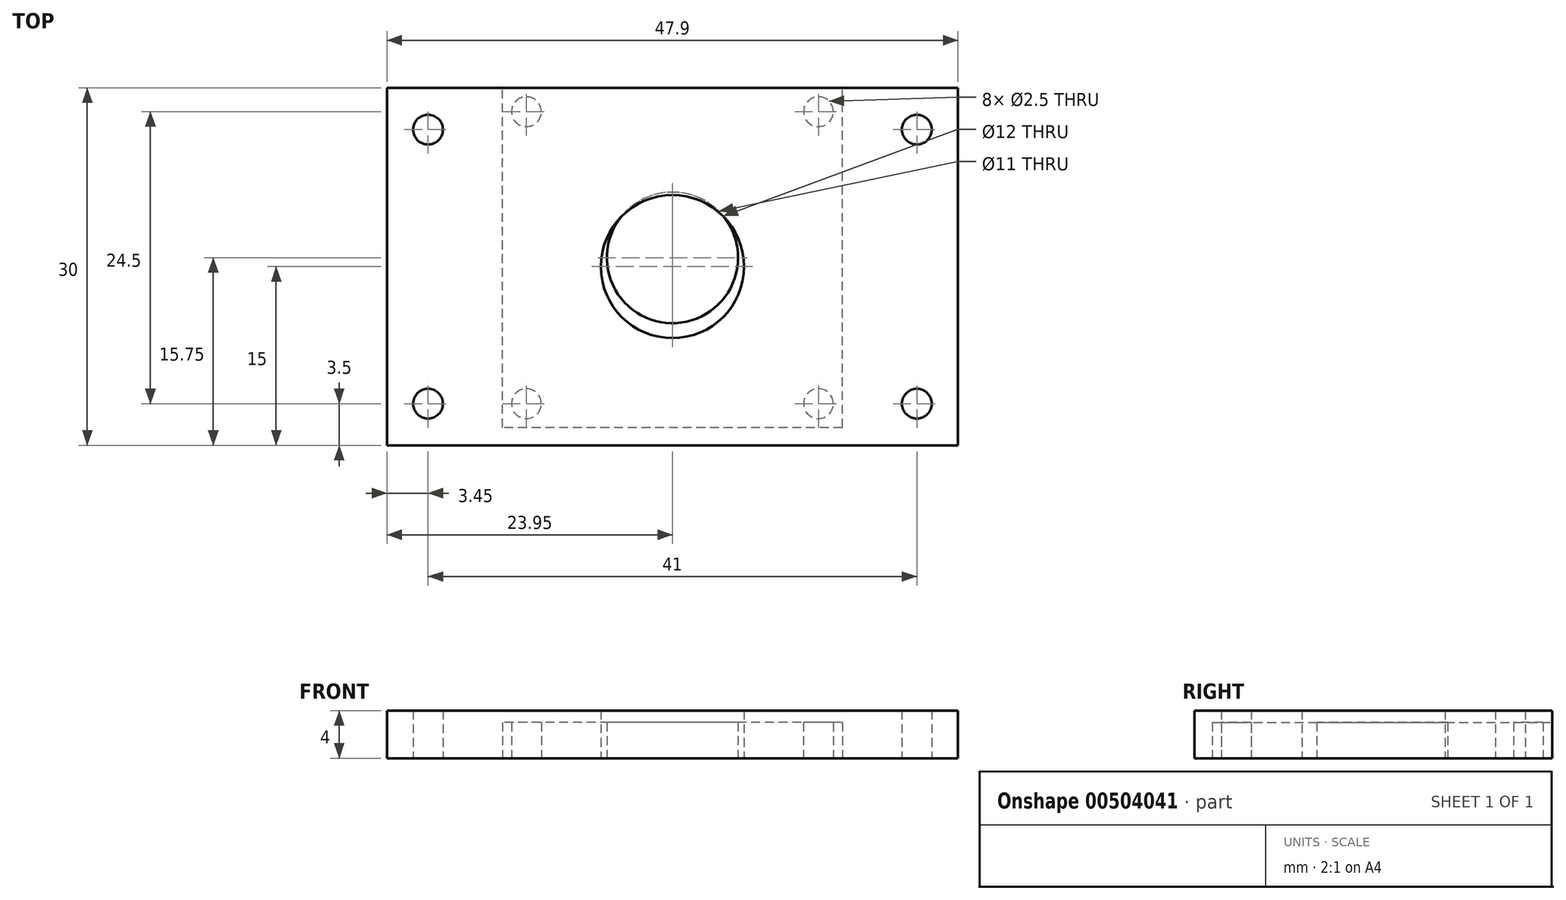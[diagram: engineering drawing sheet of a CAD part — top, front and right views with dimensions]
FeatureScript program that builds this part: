
annotation { "Feature Type Name" : "Feature", "Feature Type Description" : "" }
export const myFeature = defineFeature(function(context is Context, id is Id, definition is map)
    precondition{}
    {
        {
            var Q0;
            Q0=qCreatedBy(makeId("Top.planeOp"),FACE);
            var sketch = newSketch(context, id + "F0", { "sketchPlane" : qUnion([Q0])});
            skLineSegment(sketch, "E0.bottom", {"start": v(14.25, -14.25) * mm, "end": v(-14.25, -14.25) * mm});
            skLineSegment(sketch, "E0.top", {"start": v(14.25, 14.25) * mm, "end": v(-14.25, 14.25) * mm});
            skLineSegment(sketch, "E0.left", {"start": v(14.25, -14.25) * mm, "end": v(14.25, 14.25) * mm});
            skLineSegment(sketch, "E0.right", {"start": v(-14.25, -14.25) * mm, "end": v(-14.25, 14.25) * mm});
            skPoint(sketch, "E0.middle", {"position": v(0, 0) * mm});
            skLineSegment(sketch, "E1.bottom", {"start": v(12.25, 12.25) * mm, "end": v(-12.25, 12.25) * mm, "construction": true});
            skLineSegment(sketch, "E1.top", {"start": v(12.25, -12.25) * mm, "end": v(-12.25, -12.25) * mm, "construction": true});
            skLineSegment(sketch, "E1.left", {"start": v(12.25, 12.25) * mm, "end": v(12.25, -12.25) * mm, "construction": true});
            skLineSegment(sketch, "E1.right", {"start": v(-12.25, 12.25) * mm, "end": v(-12.25, -12.25) * mm, "construction": true});
            skCircle(sketch, "E2", {"center": v(-12.25, 12.25) * mm, "radius": 1.25 * mm});
            skCircle(sketch, "E3", {"center": v(12.25, 12.25) * mm, "radius": 1.25 * mm});
            skCircle(sketch, "E4", {"center": v(-12.25, -12.25) * mm, "radius": 1.25 * mm});
            skCircle(sketch, "E5", {"center": v(12.25, -12.25) * mm, "radius": 1.25 * mm});
            skCircle(sketch, "E6", {"center": v(0, 0) * mm, "radius": 5.5 * mm});
            skSolve(sketch);
        }
        {
            var Q0;
            Q0=makeQuery(id+"F0.imprint","IMPRINT",FACE,{"disambiguationData":[TD([[makeQuery(id+"F0.imprint","IMPRINT",EDGE,{"derivedFrom":sQuery(id+"F0.wireOp",EDGE,"E0.bottom")}),-1.0]])]});
            extrude(context, id + "F1", {"entities" : qUnion([Q0]), "depth" : 3 * mm});
        }
        {
            var Q0;
            Q0=qCreatedBy(makeId("Top.planeOp"),FACE);
            var sketch = newSketch(context, id + "F2", { "sketchPlane" : qUnion([Q0])});
            skLineSegment(sketch, "E7.bottom", {"start": v(23.95, -15.75) * mm, "end": v(-23.95, -15.75) * mm});
            skLineSegment(sketch, "E7.top", {"start": v(23.95, 14.25) * mm, "end": v(-23.95, 14.25) * mm});
            skLineSegment(sketch, "E7.left", {"start": v(23.95, -15.75) * mm, "end": v(23.95, 14.25) * mm});
            skLineSegment(sketch, "E7.right", {"start": v(-23.95, -15.75) * mm, "end": v(-23.95, 14.25) * mm});
            skPoint(sketch, "E7.middle", {"position": v(0, -0.75) * mm});
            skLineSegment(sketch, "E8.bottom", {"start": v(20.5, 10.75) * mm, "end": v(-20.5, 10.75) * mm, "construction": true});
            skLineSegment(sketch, "E8.top", {"start": v(20.5, -12.25) * mm, "end": v(-20.5, -12.25) * mm, "construction": true});
            skLineSegment(sketch, "E8.left", {"start": v(20.5, 10.75) * mm, "end": v(20.5, -12.25) * mm, "construction": true});
            skLineSegment(sketch, "E8.right", {"start": v(-20.5, 10.75) * mm, "end": v(-20.5, -12.25) * mm, "construction": true});
            skCircle(sketch, "E9", {"center": v(-20.5, 10.75) * mm, "radius": 1.25 * mm});
            skCircle(sketch, "E10", {"center": v(20.5, 10.75) * mm, "radius": 1.25 * mm});
            skCircle(sketch, "E11", {"center": v(-20.5, -12.25) * mm, "radius": 1.25 * mm});
            skCircle(sketch, "E12", {"center": v(20.5, -12.25) * mm, "radius": 1.25 * mm});
            skCircle(sketch, "E13", {"center": v(0, -0.75) * mm, "radius": 6 * mm});
            skSolve(sketch);
        }
        {
            var Q0;
            Q0=qSketchRegion(id+"F2",true);
            extrude(context, id + "F3", {"entities" : qUnion([Q0]), "depth" : 4 * mm, "offsetDistance" : 25 * mm});
        }
    });
